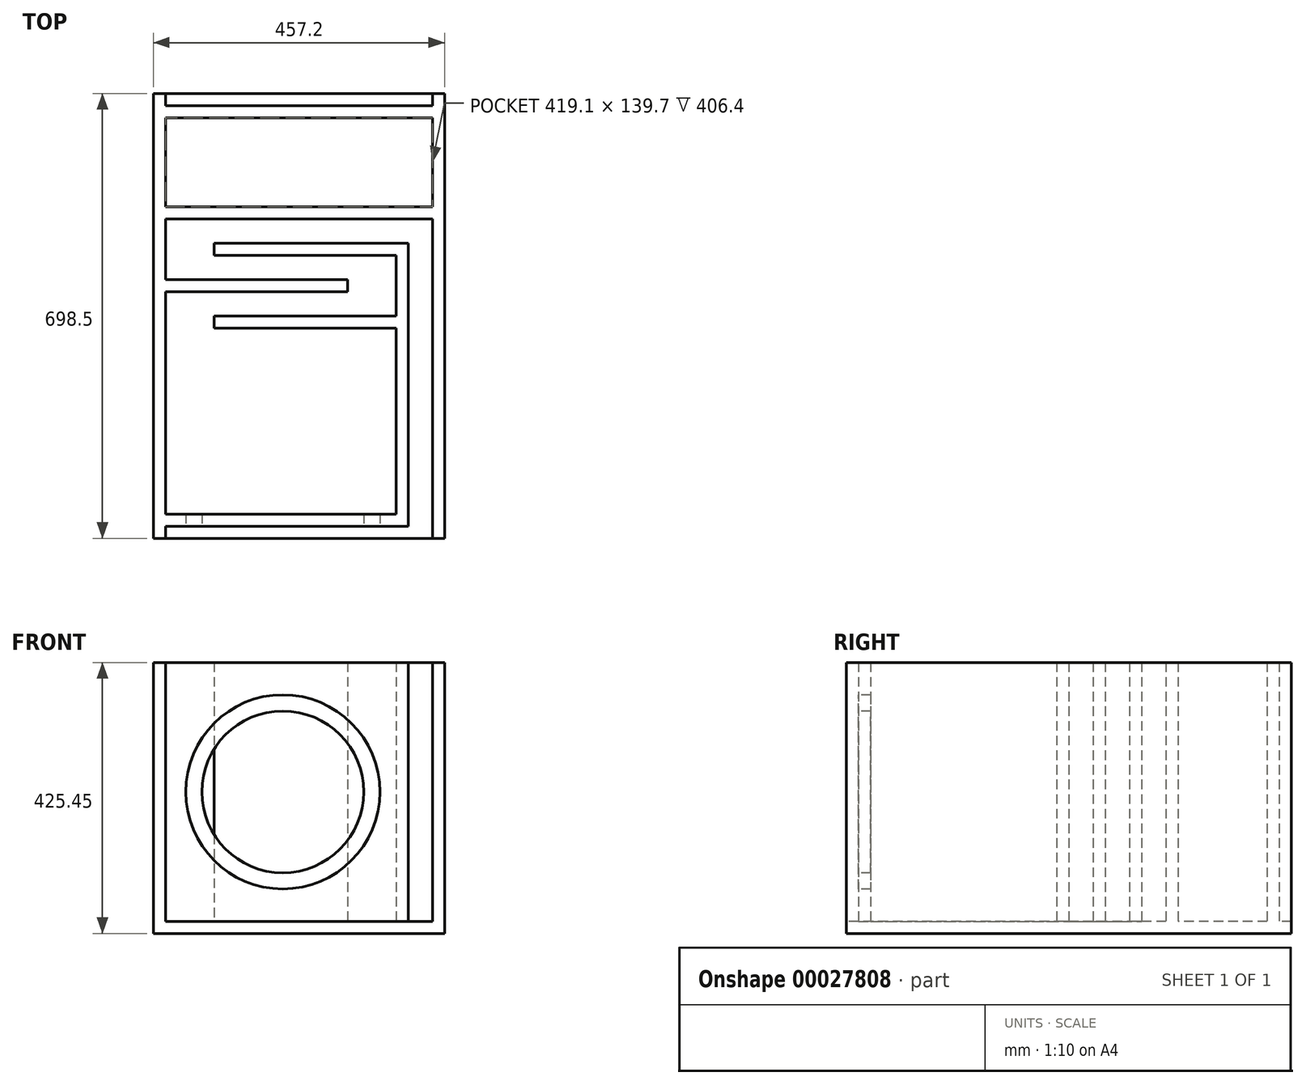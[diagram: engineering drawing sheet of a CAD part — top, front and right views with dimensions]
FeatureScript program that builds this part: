
annotation { "Feature Type Name" : "Feature", "Feature Type Description" : "" }
export const myFeature = defineFeature(function(context is Context, id is Id, definition is map)
    precondition{}
    {
        {
            var Q0;
            Q0=qCreatedBy(makeId("Top.planeOp"),FACE);
            var sketch = newSketch(context, id + "F0", { "sketchPlane" : qUnion([Q0])});
            skLineSegment(sketch, "E0.rect.bottom", {"start": v(228.6, 254) * mm, "end": v(-228.6, 254) * mm});
            skLineSegment(sketch, "E0.rect.top", {"start": v(228.6, -254) * mm, "end": v(-228.6, -254) * mm});
            skLineSegment(sketch, "E0.rect.left", {"start": v(228.6, 254) * mm, "end": v(228.6, -254) * mm});
            skLineSegment(sketch, "E0.rect.right", {"start": v(-228.6, 254) * mm, "end": v(-228.6, -254) * mm});
            skPoint(sketch, "E0.rect.middle", {"position": v(0, 0) * mm});
            skSolve(sketch);
        }
        {
            var Q0;
            Q0=makeQuery(id+"F0.imprint","IMPRINT",FACE,{"disambiguationData":[TD([[makeQuery(id+"F0.imprint","IMPRINT",EDGE,{"derivedFrom":sQuery(id+"F0.wireOp",EDGE,"E0.rect.bottom")}),1.0]])]});
            extrude(context, id + "F1", {"entities" : qUnion([Q0]), "depth" : 19.05 * mm});
        }
        {
            var Q0;
            Q0=makeQuery(id+"F1.opExtrude","CAP_FACE",FACE,{"disambiguationData":[OSD([sQuery(id+"F0.wireOp",EDGE,"E0.rect.bottom"),sQuery(id+"F0.wireOp",EDGE,"E0.rect.top"),sQuery(id+"F0.wireOp",EDGE,"E0.rect.left"),sQuery(id+"F0.wireOp",EDGE,"E0.rect.right")])],"isStart":false});
            var sketch = newSketch(context, id + "F2", { "sketchPlane" : qUnion([Q0])});
            skLineSegment(sketch, "E1.bottom", {"start": v(-228.6, 254) * mm, "end": v(-209.55, 254) * mm});
            skLineSegment(sketch, "E1.top", {"start": v(-228.6, -254) * mm, "end": v(-209.55, -254) * mm});
            skLineSegment(sketch, "E1.left", {"start": v(-228.6, 254) * mm, "end": v(-228.6, -254) * mm});
            skLineSegment(sketch, "E1.right", {"start": v(-209.55, 254) * mm, "end": v(-209.55, -254) * mm});
            skLineSegment(sketch, "E2.bottom", {"start": v(228.6, 254) * mm, "end": v(209.55, 254) * mm});
            skLineSegment(sketch, "E2.top", {"start": v(228.6, -254) * mm, "end": v(209.55, -254) * mm});
            skLineSegment(sketch, "E2.left", {"start": v(228.6, 254) * mm, "end": v(228.6, -254) * mm});
            skLineSegment(sketch, "E2.right", {"start": v(209.55, 254) * mm, "end": v(209.55, -254) * mm});
            skSolve(sketch);
        }
        {
            var Q0;
            Q0=makeQuery(id+"F2.imprint","IMPRINT",FACE,{"disambiguationData":[TD([[makeQuery(id+"F2.imprint","IMPRINT",EDGE,{"derivedFrom":sQuery(id+"F2.wireOp",EDGE,"E1.bottom")}),1.0]])]});
            var Q1;
            Q1=makeQuery(id+"F2.imprint","IMPRINT",FACE,{"disambiguationData":[TD([[makeQuery(id+"F2.imprint","IMPRINT",EDGE,{"derivedFrom":sQuery(id+"F2.wireOp",EDGE,"E2.bottom")}),1.0]])]});
            extrude(context, id + "F3", {"entities" : qUnion([Q0, Q1]), "operationType" : NewBodyOperationType.ADD, "depth" : 406.4 * mm});
        }
        {
            var Q0;
            Q0=makeQuery(id+"F1.opExtrude","CAP_FACE",FACE,{"disambiguationData":[OSD([sQuery(id+"F0.wireOp",EDGE,"E0.rect.bottom"),sQuery(id+"F0.wireOp",EDGE,"E0.rect.top"),sQuery(id+"F0.wireOp",EDGE,"E0.rect.left"),sQuery(id+"F0.wireOp",EDGE,"E0.rect.right")])],"isStart":false});
            var sketch = newSketch(context, id + "F4", { "sketchPlane" : qUnion([Q0])});
            skLineSegment(sketch, "E3.bottom", {"start": v(-209.55, 234.95) * mm, "end": v(209.55, 234.95) * mm});
            skLineSegment(sketch, "E3.top", {"start": v(-209.55, 215.9) * mm, "end": v(209.55, 215.9) * mm});
            skLineSegment(sketch, "E3.left", {"start": v(-209.55, 234.95) * mm, "end": v(-209.55, 215.9) * mm});
            skLineSegment(sketch, "E3.right", {"start": v(209.55, 234.95) * mm, "end": v(209.55, 215.9) * mm});
            skSolve(sketch);
        }
        {
            var Q0;
            Q0=makeQuery(id+"F4.imprint","IMPRINT",FACE,{"disambiguationData":[TD([[makeQuery(id+"F4.imprint","IMPRINT",EDGE,{"derivedFrom":sQuery(id+"F4.wireOp",EDGE,"E3.bottom")}),-1.0]])]});
            extrude(context, id + "F5", {"entities" : qUnion([Q0]), "operationType" : NewBodyOperationType.ADD, "depth" : 406.4 * mm});
        }
        {
            var Q0;
            {var subQ0=sQuery(id+"F0.wireOp",EDGE,"E0.rect.top");Q0=makeQuery(id+"F5.boolean.opBoolean","SPLIT",FACE,{"disambiguationData":[TD([makeQuery(id+"F1.opExtrude","SWEPT_FACE",FACE,{"disambiguationData":[OSD([subQ0])]})])],"derivedFrom":makeQuery(id+"F1.opExtrude","CAP_FACE",FACE,{"disambiguationData":[OSD([sQuery(id+"F0.wireOp",EDGE,"E0.rect.bottom"),subQ0,sQuery(id+"F0.wireOp",EDGE,"E0.rect.left"),sQuery(id+"F0.wireOp",EDGE,"E0.rect.right")])],"isStart":false})});}
            var sketch = newSketch(context, id + "F6", { "sketchPlane" : qUnion([Q0])});
            skLineSegment(sketch, "E4.bottom", {"start": v(-209.55, -215.9) * mm, "end": v(209.55, -215.9) * mm});
            skLineSegment(sketch, "E4.top", {"start": v(-209.55, -234.95) * mm, "end": v(209.55, -234.95) * mm});
            skLineSegment(sketch, "E4.left", {"start": v(-209.55, -215.9) * mm, "end": v(-209.55, -234.95) * mm});
            skLineSegment(sketch, "E4.right", {"start": v(209.55, -215.9) * mm, "end": v(209.55, -234.95) * mm});
            skSolve(sketch);
        }
        {
            var Q0;
            Q0=makeQuery(id+"F6.imprint","IMPRINT",FACE,{"disambiguationData":[TD([[makeQuery(id+"F6.imprint","IMPRINT",EDGE,{"derivedFrom":sQuery(id+"F6.wireOp",EDGE,"E4.bottom")}),-1.0]])]});
            extrude(context, id + "F7", {"entities" : qUnion([Q0]), "operationType" : NewBodyOperationType.ADD, "depth" : 406.4 * mm});
        }
        {
            var Q0;
            {var subQ0=sQuery(id+"F0.wireOp",EDGE,"E0.rect.top");var subQ1=makeQuery(id+"F5.opExtrude","SWEPT_FACE",FACE,{"disambiguationData":[OSD([sQuery(id+"F4.wireOp",EDGE,"E3.top")])]});Q0=makeQuery(id+"F7.boolean.opBoolean","SPLIT",FACE,{"disambiguationData":[TD([subQ1])],"derivedFrom":makeQuery(id+"F5.boolean.opBoolean","SPLIT",FACE,{"disambiguationData":[TD([makeQuery(id+"F1.opExtrude","SWEPT_FACE",FACE,{"disambiguationData":[OSD([subQ0])]})])],"derivedFrom":makeQuery(id+"F1.opExtrude","CAP_FACE",FACE,{"disambiguationData":[OSD([sQuery(id+"F0.wireOp",EDGE,"E0.rect.bottom"),subQ0,sQuery(id+"F0.wireOp",EDGE,"E0.rect.left"),sQuery(id+"F0.wireOp",EDGE,"E0.rect.right")])],"isStart":false})})});}
            var sketch = newSketch(context, id + "F8", { "sketchPlane" : qUnion([Q0])});
            skLineSegment(sketch, "E5.bottom", {"start": v(171.45, -215.9) * mm, "end": v(152.4, -215.9) * mm});
            skLineSegment(sketch, "E5.top", {"start": v(171.45, 82.55) * mm, "end": v(152.4, 82.55) * mm});
            skLineSegment(sketch, "E5.left", {"start": v(171.45, -215.9) * mm, "end": v(171.45, 82.55) * mm});
            skLineSegment(sketch, "E5.right", {"start": v(152.4, -215.9) * mm, "end": v(152.4, 82.55) * mm});
            skLineSegment(sketch, "E6.bottom", {"start": v(152.4, 82.55) * mm, "end": v(-133.35, 82.55) * mm});
            skLineSegment(sketch, "E6.top", {"start": v(152.4, 63.5) * mm, "end": v(-133.35, 63.5) * mm});
            skLineSegment(sketch, "E6.left", {"start": v(152.4, 82.55) * mm, "end": v(152.4, 63.5) * mm});
            skLineSegment(sketch, "E6.right", {"start": v(-133.35, 82.55) * mm, "end": v(-133.35, 63.5) * mm});
            skLineSegment(sketch, "E7.bottom", {"start": v(-209.55, 25.4) * mm, "end": v(76.2, 25.4) * mm});
            skLineSegment(sketch, "E7.top", {"start": v(-209.55, 6.35) * mm, "end": v(76.2, 6.35) * mm});
            skLineSegment(sketch, "E7.left", {"start": v(-209.55, 25.4) * mm, "end": v(-209.55, 6.35) * mm});
            skLineSegment(sketch, "E7.right", {"start": v(76.2, 25.4) * mm, "end": v(76.2, 6.35) * mm});
            skLineSegment(sketch, "E8.bottom", {"start": v(152.4, -31.75) * mm, "end": v(-133.35, -31.75) * mm});
            skLineSegment(sketch, "E8.top", {"start": v(152.4, -50.8) * mm, "end": v(-133.35, -50.8) * mm});
            skLineSegment(sketch, "E8.left", {"start": v(152.4, -31.75) * mm, "end": v(152.4, -50.8) * mm});
            skLineSegment(sketch, "E8.right", {"start": v(-133.35, -31.75) * mm, "end": v(-133.35, -50.8) * mm});
            skSolve(sketch);
        }
        {
            var Q0;
            Q0=makeQuery(id+"F8.imprint","IMPRINT",FACE,{"disambiguationData":[TD([[makeQuery(id+"F8.imprint","IMPRINT",EDGE,{"derivedFrom":sQuery(id+"F8.wireOp",EDGE,"E6.bottom")}),1.0]])]});
            var Q1;
            Q1=makeQuery(id+"F8.imprint","IMPRINT",FACE,{"disambiguationData":[TD([[makeQuery(id+"F8.imprint","IMPRINT",EDGE,{"derivedFrom":sQuery(id+"F8.wireOp",EDGE,"E7.bottom")}),-1.0]])]});
            var Q2;
            Q2=makeQuery(id+"F8.imprint","IMPRINT",FACE,{"disambiguationData":[TD([[makeQuery(id+"F8.imprint","IMPRINT",EDGE,{"derivedFrom":sQuery(id+"F8.wireOp",EDGE,"E8.bottom")}),1.0]])]});
            var Q3;
            {var subQ3=sQuery(id+"F8.wireOp",EDGE,"E5.bottom");Q3=makeQuery(id+"F8.imprint","IMPRINT",FACE,{"disambiguationData":[TD([[makeQuery(id+"F8.imprint","IMPRINT",EDGE,{"derivedFrom":subQ3}),1.0]])]});}
            extrude(context, id + "F9", {"entities" : qUnion([Q0, Q1, Q2, Q3]), "operationType" : NewBodyOperationType.ADD, "depth" : 406.4 * mm});
        }
        {
            var Q0;
            Q0=makeQuery(id+"F9.boolean.opBoolean","MERGE",FACE,{"derivedFrom":[makeQuery(id+"F7.boolean.opBoolean","MERGE",FACE,{"derivedFrom":[makeQuery(id+"F5.boolean.opBoolean","MERGE",FACE,{"derivedFrom":[makeQuery(id+"F3.opExtrude","CAP_FACE",FACE,{"disambiguationData":[OSD([sQuery(id+"F2.wireOp",EDGE,"E1.bottom"),sQuery(id+"F2.wireOp",EDGE,"E1.top"),sQuery(id+"F2.wireOp",EDGE,"E1.left"),sQuery(id+"F2.wireOp",EDGE,"E1.right")])],"isStart":false}),makeQuery(id+"F3.opExtrude","CAP_FACE",FACE,{"disambiguationData":[OSD([sQuery(id+"F2.wireOp",EDGE,"E2.bottom"),sQuery(id+"F2.wireOp",EDGE,"E2.top"),sQuery(id+"F2.wireOp",EDGE,"E2.left"),sQuery(id+"F2.wireOp",EDGE,"E2.right")])],"isStart":false}),makeQuery(id+"F5.opExtrude","CAP_FACE",FACE,{"disambiguationData":[OSD([sQuery(id+"F4.wireOp",EDGE,"E3.bottom"),sQuery(id+"F4.wireOp",EDGE,"E3.top"),sQuery(id+"F4.wireOp",EDGE,"E3.left"),sQuery(id+"F4.wireOp",EDGE,"E3.right")])],"isStart":false})]}),makeQuery(id+"F7.opExtrude","CAP_FACE",FACE,{"disambiguationData":[OSD([sQuery(id+"F6.wireOp",EDGE,"E4.bottom"),sQuery(id+"F6.wireOp",EDGE,"E4.top"),sQuery(id+"F6.wireOp",EDGE,"E4.left"),sQuery(id+"F6.wireOp",EDGE,"E4.right")])],"isStart":false})]}),makeQuery(id+"F9.opExtrude","CAP_FACE",FACE,{"disambiguationData":[OSD([sQuery(id+"F8.wireOp",EDGE,"E5.bottom"),sQuery(id+"F8.wireOp",EDGE,"E5.top"),sQuery(id+"F8.wireOp",EDGE,"E5.left"),sQuery(id+"F8.wireOp",EDGE,"E5.right"),sQuery(id+"F8.wireOp",EDGE,"E6.bottom"),sQuery(id+"F8.wireOp",EDGE,"E6.top"),sQuery(id+"F8.wireOp",EDGE,"E6.right"),sQuery(id+"F8.wireOp",EDGE,"E8.bottom"),sQuery(id+"F8.wireOp",EDGE,"E8.top"),sQuery(id+"F8.wireOp",EDGE,"E8.right")])],"isStart":false}),makeQuery(id+"F9.opExtrude","CAP_FACE",FACE,{"disambiguationData":[OSD([sQuery(id+"F8.wireOp",EDGE,"E7.bottom"),sQuery(id+"F8.wireOp",EDGE,"E7.top"),sQuery(id+"F8.wireOp",EDGE,"E7.left"),sQuery(id+"F8.wireOp",EDGE,"E7.right")])],"isStart":false})]});
            var sketch = newSketch(context, id + "F10", { "sketchPlane" : qUnion([Q0])});
            skLineSegment(sketch, "E9.bottom", {"start": v(-209.55, -215.9) * mm, "end": v(209.55, -215.9) * mm});
            skLineSegment(sketch, "E9.top", {"start": v(-209.55, -234.95) * mm, "end": v(209.55, -234.95) * mm});
            skLineSegment(sketch, "E9.left", {"start": v(-209.55, -215.9) * mm, "end": v(-209.55, -234.95) * mm});
            skLineSegment(sketch, "E9.right", {"start": v(209.55, -215.9) * mm, "end": v(209.55, -234.95) * mm});
            skSolve(sketch);
        }
        {
            var Q0;
            Q0=makeQuery(id+"F10.imprint","IMPRINT",FACE,{"disambiguationData":[TD([[makeQuery(id+"F10.imprint","IMPRINT",EDGE,{"derivedFrom":sQuery(id+"F10.wireOp",EDGE,"E9.top")}),1.0]])]});
            extrude(context, id + "F11", {"entities" : qUnion([Q0]), "operationType" : NewBodyOperationType.REMOVE, "oppositeDirection" : true, "depth" : 406.4 * mm});
        }
        {
            var Q0;
            Q0=makeQuery(id+"F3.boolean.opBoolean","MERGE",FACE,{"derivedFrom":[makeQuery(id+"F1.opExtrude","SWEPT_FACE",FACE,{"disambiguationData":[OSD([sQuery(id+"F0.wireOp",EDGE,"E0.rect.top")])]}),makeQuery(id+"F3.opExtrude","SWEPT_FACE",FACE,{"disambiguationData":[OSD([sQuery(id+"F2.wireOp",EDGE,"E1.top")])]}),makeQuery(id+"F3.opExtrude","SWEPT_FACE",FACE,{"disambiguationData":[OSD([sQuery(id+"F2.wireOp",EDGE,"E2.top")])]})]});
            extrude(context, id + "F12", {"entities" : qUnion([Q0]), "operationType" : NewBodyOperationType.ADD, "depth" : 127 * mm});
        }
        {
            var Q0;
            Q0=makeQuery(id+"F11.boolean.opBoolean","COPY",FACE,{"derivedFrom":makeQuery(id+"F11.opExtrude","SWEPT_FACE",FACE,{"disambiguationData":[OSD([sQuery(id+"F10.wireOp",EDGE,"E9.bottom")])]})});
            extrude(context, id + "F13", {"entities" : qUnion([Q0]), "operationType" : NewBodyOperationType.ADD, "depth" : 127 * mm});
        }
        {
            var Q0;
            {var subQ0=sQuery(id+"F0.wireOp",EDGE,"E0.rect.top");var subQ1=makeQuery(id+"F5.opExtrude","SWEPT_FACE",FACE,{"disambiguationData":[OSD([sQuery(id+"F4.wireOp",EDGE,"E3.top")])]});var subQ6=makeQuery(id+"F1.opExtrude","SWEPT_FACE",FACE,{"disambiguationData":[OSD([subQ0])]});var subQ7=makeQuery(id+"F5.boolean.opBoolean","SPLIT",FACE,{"disambiguationData":[TD([subQ6])],"derivedFrom":makeQuery(id+"F1.opExtrude","CAP_FACE",FACE,{"disambiguationData":[OSD([sQuery(id+"F0.wireOp",EDGE,"E0.rect.bottom"),subQ0,sQuery(id+"F0.wireOp",EDGE,"E0.rect.left"),sQuery(id+"F0.wireOp",EDGE,"E0.rect.right")])],"isStart":false})});Q0=makeQuery(id+"F12.boolean.opBoolean","MERGE",FACE,{"derivedFrom":[makeQuery(id+"F11.boolean.opBoolean","MERGE",FACE,{"derivedFrom":[makeQuery(id+"F7.boolean.opBoolean","SPLIT",FACE,{"disambiguationData":[TD([subQ6])],"derivedFrom":subQ7}),makeQuery(id+"F7.boolean.opBoolean","SPLIT",FACE,{"disambiguationData":[TD([subQ1])],"derivedFrom":subQ7}),makeQuery(id+"F11.opExtrude","CAP_FACE",FACE,{"disambiguationData":[OSD([sQuery(id+"F10.wireOp",EDGE,"E9.bottom"),sQuery(id+"F10.wireOp",EDGE,"E9.top"),sQuery(id+"F10.wireOp",EDGE,"E9.left"),sQuery(id+"F10.wireOp",EDGE,"E9.right")])],"isStart":false})]}),makeQuery(id+"F12.opExtrude","SWEPT_FACE",FACE,{"disambiguationData":[OSD([subQ0]),TDD([makeQuery(id+"F1.opExtrude","CAP_EDGE",EDGE,{"disambiguationData":[OSD([subQ0])],"isStart":false})])]})]});}
            var sketch = newSketch(context, id + "F14", { "sketchPlane" : qUnion([Q0])});
            skLineSegment(sketch, "E10.bottom", {"start": v(171.45, -342.9) * mm, "end": v(-209.55, -342.9) * mm});
            skLineSegment(sketch, "E10.top", {"start": v(171.45, -361.95) * mm, "end": v(-209.55, -361.95) * mm});
            skLineSegment(sketch, "E10.left", {"start": v(171.45, -342.9) * mm, "end": v(171.45, -361.95) * mm});
            skLineSegment(sketch, "E10.right", {"start": v(-209.55, -342.9) * mm, "end": v(-209.55, -361.95) * mm});
            skSolve(sketch);
        }
        {
            var Q0;
            Q0=makeQuery(id+"F14.imprint","IMPRINT",FACE,{"disambiguationData":[TD([[makeQuery(id+"F14.imprint","IMPRINT",EDGE,{"derivedFrom":sQuery(id+"F14.wireOp",EDGE,"E10.top")}),-1.0]])]});
            extrude(context, id + "F15", {"entities" : qUnion([Q0]), "operationType" : NewBodyOperationType.ADD, "depth" : 406.4 * mm});
        }
        {
            var Q0;
            Q0=makeQuery(id+"F15.opExtrude","SWEPT_FACE",FACE,{"disambiguationData":[OSD([sQuery(id+"F14.wireOp",EDGE,"E10.top")])]});
            var sketch = newSketch(context, id + "F16", { "sketchPlane" : qUnion([Q0])});
            skCircle(sketch, "E11", {"center": v(-25.4, 222.25) * mm, "radius": 152.4 * mm});
            skSolve(sketch);
        }
        {
            var Q0;
            Q0=makeQuery(id+"F16.imprint","IMPRINT",FACE,{"disambiguationData":[TD([[makeQuery(id+"F16.imprint","IMPRINT",EDGE,{"derivedFrom":sQuery(id+"F16.wireOp",EDGE,"E11")}),1.0]])]});
            extrude(context, id + "F17", {"entities" : qUnion([Q0]), "operationType" : NewBodyOperationType.REMOVE, "oppositeDirection" : true, "depth" : 25.4 * mm});
        }
        {
            var Q0;
            Q0=makeQuery(id+"F5.opExtrude","SWEPT_FACE",FACE,{"disambiguationData":[OSD([sQuery(id+"F4.wireOp",EDGE,"E3.bottom")])]});
            var sketch = newSketch(context, id + "F18", { "sketchPlane" : qUnion([Q0])});
            skLineSegment(sketch, "E12.rect.bottom", {"start": v(-107.95, 349.25) * mm, "end": v(107.95, 349.25) * mm});
            skLineSegment(sketch, "E12.rect.top", {"start": v(-107.95, 133.35) * mm, "end": v(107.95, 133.35) * mm});
            skLineSegment(sketch, "E12.rect.left", {"start": v(-107.95, 349.25) * mm, "end": v(-107.95, 133.35) * mm});
            skLineSegment(sketch, "E12.rect.right", {"start": v(107.95, 349.25) * mm, "end": v(107.95, 133.35) * mm});
            skPoint(sketch, "E12.rect.middle", {"position": v(0, 241.3) * mm});
            skSolve(sketch);
        }
        {
            var Q0;
            Q0=makeQuery(id+"F18.imprint","IMPRINT",FACE,{"disambiguationData":[TD([[makeQuery(id+"F18.imprint","IMPRINT",EDGE,{"derivedFrom":sQuery(id+"F18.wireOp",EDGE,"E12.rect.bottom")}),-1.0]])]});
            extrude(context, id + "F19", {"entities" : qUnion([Q0]), "operationType" : NewBodyOperationType.REMOVE, "oppositeDirection" : true, "depth" : 25.4 * mm});
        }
        {
            var Q0;
            {var subQ0=sQuery(id+"F0.wireOp",EDGE,"E0.rect.top");var subQ1=makeQuery(id+"F5.opExtrude","SWEPT_FACE",FACE,{"disambiguationData":[OSD([sQuery(id+"F4.wireOp",EDGE,"E3.top")])]});var subQ6=makeQuery(id+"F1.opExtrude","SWEPT_FACE",FACE,{"disambiguationData":[OSD([subQ0])]});var subQ7=makeQuery(id+"F5.boolean.opBoolean","SPLIT",FACE,{"disambiguationData":[TD([subQ6])],"derivedFrom":makeQuery(id+"F1.opExtrude","CAP_FACE",FACE,{"disambiguationData":[OSD([sQuery(id+"F0.wireOp",EDGE,"E0.rect.bottom"),subQ0,sQuery(id+"F0.wireOp",EDGE,"E0.rect.left"),sQuery(id+"F0.wireOp",EDGE,"E0.rect.right")])],"isStart":false})});Q0=makeQuery(id+"F12.boolean.opBoolean","MERGE",FACE,{"derivedFrom":[makeQuery(id+"F11.boolean.opBoolean","MERGE",FACE,{"derivedFrom":[makeQuery(id+"F7.boolean.opBoolean","SPLIT",FACE,{"disambiguationData":[TD([subQ6])],"derivedFrom":subQ7}),makeQuery(id+"F7.boolean.opBoolean","SPLIT",FACE,{"disambiguationData":[TD([subQ1])],"derivedFrom":subQ7}),makeQuery(id+"F11.opExtrude","CAP_FACE",FACE,{"disambiguationData":[OSD([sQuery(id+"F10.wireOp",EDGE,"E9.bottom"),sQuery(id+"F10.wireOp",EDGE,"E9.top"),sQuery(id+"F10.wireOp",EDGE,"E9.left"),sQuery(id+"F10.wireOp",EDGE,"E9.right")])],"isStart":false})]}),makeQuery(id+"F12.opExtrude","SWEPT_FACE",FACE,{"disambiguationData":[OSD([subQ0]),TDD([makeQuery(id+"F1.opExtrude","CAP_EDGE",EDGE,{"disambiguationData":[OSD([subQ0])],"isStart":false})])]})]});}
            var sketch = newSketch(context, id + "F20", { "sketchPlane" : qUnion([Q0])});
            skLineSegment(sketch, "E13.bottom", {"start": v(-209.55, 120.65) * mm, "end": v(209.55, 120.65) * mm});
            skLineSegment(sketch, "E13.top", {"start": v(-209.55, 139.7) * mm, "end": v(209.55, 139.7) * mm});
            skLineSegment(sketch, "E13.left", {"start": v(-209.55, 120.65) * mm, "end": v(-209.55, 139.7) * mm});
            skLineSegment(sketch, "E13.right", {"start": v(209.55, 120.65) * mm, "end": v(209.55, 139.7) * mm});
            skSolve(sketch);
        }
        {
            var Q0;
            Q0=makeQuery(id+"F20.imprint","IMPRINT",FACE,{"disambiguationData":[TD([[makeQuery(id+"F20.imprint","IMPRINT",EDGE,{"derivedFrom":sQuery(id+"F20.wireOp",EDGE,"E13.bottom")}),1.0]])]});
            extrude(context, id + "F21", {"entities" : qUnion([Q0]), "operationType" : NewBodyOperationType.ADD, "depth" : 406.4 * mm});
        }
        {
            var Q0;
            {var subQ0=sQuery(id+"F2.wireOp",EDGE,"E1.bottom");var subQ1=sQuery(id+"F2.wireOp",EDGE,"E1.top");var subQ2=sQuery(id+"F2.wireOp",EDGE,"E1.left");var subQ3=sQuery(id+"F2.wireOp",EDGE,"E1.right");var subQ4=sQuery(id+"F2.wireOp",EDGE,"E2.bottom");var subQ5=sQuery(id+"F2.wireOp",EDGE,"E2.top");var subQ6=sQuery(id+"F2.wireOp",EDGE,"E2.left");var subQ7=sQuery(id+"F2.wireOp",EDGE,"E2.right");var subQ8=sQuery(id+"F4.wireOp",EDGE,"E3.bottom");var subQ9=sQuery(id+"F4.wireOp",EDGE,"E3.top");var subQ10=sQuery(id+"F6.wireOp",EDGE,"E4.bottom");var subQ11=sQuery(id+"F8.wireOp",EDGE,"E5.bottom");var subQ12=sQuery(id+"F8.wireOp",EDGE,"E5.top");var subQ13=sQuery(id+"F8.wireOp",EDGE,"E5.left");var subQ14=sQuery(id+"F8.wireOp",EDGE,"E5.right");var subQ15=sQuery(id+"F8.wireOp",EDGE,"E6.bottom");var subQ16=sQuery(id+"F8.wireOp",EDGE,"E6.top");var subQ17=sQuery(id+"F8.wireOp",EDGE,"E6.right");var subQ18=sQuery(id+"F8.wireOp",EDGE,"E8.bottom");var subQ19=sQuery(id+"F8.wireOp",EDGE,"E8.top");var subQ20=sQuery(id+"F8.wireOp",EDGE,"E8.right");var subQ21=sQuery(id+"F8.wireOp",EDGE,"E7.bottom");var subQ22=sQuery(id+"F8.wireOp",EDGE,"E7.top");var subQ23=sQuery(id+"F8.wireOp",EDGE,"E7.right");var subQ24=makeQuery(id+"F9.boolean.opBoolean","MERGE",FACE,{"derivedFrom":[makeQuery(id+"F7.boolean.opBoolean","MERGE",FACE,{"derivedFrom":[makeQuery(id+"F5.boolean.opBoolean","MERGE",FACE,{"derivedFrom":[makeQuery(id+"F3.opExtrude","CAP_FACE",FACE,{"disambiguationData":[OSD([subQ0,subQ1,subQ2,subQ3])],"isStart":false}),makeQuery(id+"F3.opExtrude","CAP_FACE",FACE,{"disambiguationData":[OSD([subQ4,subQ5,subQ6,subQ7])],"isStart":false}),makeQuery(id+"F5.opExtrude","CAP_FACE",FACE,{"disambiguationData":[OSD([subQ8,subQ9,sQuery(id+"F4.wireOp",EDGE,"E3.left"),sQuery(id+"F4.wireOp",EDGE,"E3.right")])],"isStart":false})]}),makeQuery(id+"F7.opExtrude","CAP_FACE",FACE,{"disambiguationData":[OSD([subQ10,sQuery(id+"F6.wireOp",EDGE,"E4.top"),sQuery(id+"F6.wireOp",EDGE,"E4.left"),sQuery(id+"F6.wireOp",EDGE,"E4.right")])],"isStart":false})]}),makeQuery(id+"F9.opExtrude","CAP_FACE",FACE,{"disambiguationData":[OSD([subQ11,subQ12,subQ13,subQ14,subQ15,subQ16,subQ17,subQ18,subQ19,subQ20])],"isStart":false}),makeQuery(id+"F9.opExtrude","CAP_FACE",FACE,{"disambiguationData":[OSD([subQ21,subQ22,sQuery(id+"F8.wireOp",EDGE,"E7.left"),subQ23])],"isStart":false})]});var subQ25=sQuery(id+"F10.wireOp",EDGE,"E9.bottom");Q0=makeQuery(id+"F21.boolean.opBoolean","MERGE",FACE,{"derivedFrom":[makeQuery(id+"F15.boolean.opBoolean","MERGE",FACE,{"derivedFrom":[makeQuery(id+"F12.boolean.opBoolean","MERGE",FACE,{"derivedFrom":[makeQuery(id+"F11.boolean.opBoolean","SPLIT",FACE,{"disambiguationData":[TD([makeQuery(id+"F1.opExtrude","SWEPT_FACE",FACE,{"disambiguationData":[OSD([sQuery(id+"F0.wireOp",EDGE,"E0.rect.bottom")])]})])],"derivedFrom":subQ24}),makeQuery(id+"F12.opExtrude","SWEPT_FACE",FACE,{"disambiguationData":[OSD([subQ1])]}),makeQuery(id+"F12.opExtrude","SWEPT_FACE",FACE,{"disambiguationData":[OSD([subQ5])]})]}),makeQuery(id+"F13.boolean.opBoolean","MERGE",FACE,{"derivedFrom":[makeQuery(id+"F11.boolean.opBoolean","SPLIT",FACE,{"disambiguationData":[TD([makeQuery(id+"F9.opExtrude","SWEPT_FACE",FACE,{"disambiguationData":[OSD([subQ13])]})])],"derivedFrom":subQ24}),makeQuery(id+"F13.opExtrude","SWEPT_FACE",FACE,{"disambiguationData":[OSD([subQ25]),TDD([makeQuery(id+"F11.boolean.opBoolean","COPY",EDGE,{"derivedFrom":makeQuery(id+"F11.opExtrude","CAP_EDGE",EDGE,{"disambiguationData":[OSD([subQ25])],"isStart":true})})])]})]}),makeQuery(id+"F15.opExtrude","CAP_FACE",FACE,{"disambiguationData":[OSD([sQuery(id+"F14.wireOp",EDGE,"E10.bottom"),sQuery(id+"F14.wireOp",EDGE,"E10.top"),sQuery(id+"F14.wireOp",EDGE,"E10.left"),sQuery(id+"F14.wireOp",EDGE,"E10.right")])],"isStart":false})]}),makeQuery(id+"F21.opExtrude","CAP_FACE",FACE,{"disambiguationData":[OSD([sQuery(id+"F20.wireOp",EDGE,"E13.bottom"),sQuery(id+"F20.wireOp",EDGE,"E13.top"),sQuery(id+"F20.wireOp",EDGE,"E13.left"),sQuery(id+"F20.wireOp",EDGE,"E13.right")])],"isStart":false})]});}
            var sketch = newSketch(context, id + "F22", { "sketchPlane" : qUnion([Q0])});
            skLineSegment(sketch, "E14.bottom", {"start": v(-209.55, 234.95) * mm, "end": v(209.55, 234.95) * mm});
            skLineSegment(sketch, "E14.top", {"start": v(-209.55, 215.9) * mm, "end": v(209.55, 215.9) * mm});
            skLineSegment(sketch, "E14.left", {"start": v(-209.55, 234.95) * mm, "end": v(-209.55, 215.9) * mm});
            skLineSegment(sketch, "E14.right", {"start": v(209.55, 234.95) * mm, "end": v(209.55, 215.9) * mm});
            skSolve(sketch);
        }
        {
            var Q0;
            Q0=makeQuery(id+"F22.imprint","IMPRINT",FACE,{"disambiguationData":[TD([[makeQuery(id+"F22.imprint","IMPRINT",EDGE,{"derivedFrom":sQuery(id+"F22.wireOp",EDGE,"E14.bottom")}),-1.0]])]});
            extrude(context, id + "F23", {"entities" : qUnion([Q0]), "operationType" : NewBodyOperationType.REMOVE, "oppositeDirection" : true, "depth" : 406.4 * mm});
        }
        {
            var Q0;
            Q0=makeQuery(id+"F3.boolean.opBoolean","MERGE",FACE,{"derivedFrom":[makeQuery(id+"F1.opExtrude","SWEPT_FACE",FACE,{"disambiguationData":[OSD([sQuery(id+"F0.wireOp",EDGE,"E0.rect.bottom")])]}),makeQuery(id+"F3.opExtrude","SWEPT_FACE",FACE,{"disambiguationData":[OSD([sQuery(id+"F2.wireOp",EDGE,"E1.bottom")])]}),makeQuery(id+"F3.opExtrude","SWEPT_FACE",FACE,{"disambiguationData":[OSD([sQuery(id+"F2.wireOp",EDGE,"E2.bottom")])]})]});
            extrude(context, id + "F24", {"entities" : qUnion([Q0]), "operationType" : NewBodyOperationType.ADD, "depth" : 63.5 * mm});
        }
        {
            var Q0;
            {var subQ0=sQuery(id+"F0.wireOp",EDGE,"E0.rect.bottom");var subQ1=sQuery(id+"F0.wireOp",EDGE,"E0.rect.top");var subQ2=makeQuery(id+"F1.opExtrude","CAP_FACE",FACE,{"disambiguationData":[OSD([subQ0,subQ1,sQuery(id+"F0.wireOp",EDGE,"E0.rect.left"),sQuery(id+"F0.wireOp",EDGE,"E0.rect.right")])],"isStart":false});var subQ6=makeQuery(id+"F5.opExtrude","SWEPT_FACE",FACE,{"disambiguationData":[OSD([sQuery(id+"F4.wireOp",EDGE,"E3.top")])]});var subQ10=makeQuery(id+"F1.opExtrude","SWEPT_FACE",FACE,{"disambiguationData":[OSD([subQ1])]});var subQ11=makeQuery(id+"F5.boolean.opBoolean","SPLIT",FACE,{"disambiguationData":[TD([subQ10])],"derivedFrom":subQ2});var subQ12=sQuery(id+"F10.wireOp",EDGE,"E9.right");Q0=makeQuery(id+"F24.boolean.opBoolean","MERGE",FACE,{"derivedFrom":[makeQuery(id+"F23.boolean.opBoolean","MERGE",FACE,{"derivedFrom":[makeQuery(id+"F5.boolean.opBoolean","SPLIT",FACE,{"disambiguationData":[TD([makeQuery(id+"F1.opExtrude","SWEPT_FACE",FACE,{"disambiguationData":[OSD([subQ0])]})])],"derivedFrom":subQ2}),makeQuery(id+"F21.boolean.opBoolean","SPLIT",FACE,{"disambiguationData":[TD([subQ6])],"derivedFrom":makeQuery(id+"F12.boolean.opBoolean","MERGE",FACE,{"derivedFrom":[makeQuery(id+"F11.boolean.opBoolean","MERGE",FACE,{"derivedFrom":[makeQuery(id+"F7.boolean.opBoolean","SPLIT",FACE,{"disambiguationData":[TD([subQ10])],"derivedFrom":subQ11}),makeQuery(id+"F7.boolean.opBoolean","SPLIT",FACE,{"disambiguationData":[TD([subQ6])],"derivedFrom":subQ11}),makeQuery(id+"F11.opExtrude","CAP_FACE",FACE,{"disambiguationData":[OSD([sQuery(id+"F10.wireOp",EDGE,"E9.bottom"),sQuery(id+"F10.wireOp",EDGE,"E9.top"),sQuery(id+"F10.wireOp",EDGE,"E9.left"),subQ12])],"isStart":false})]}),makeQuery(id+"F12.opExtrude","SWEPT_FACE",FACE,{"disambiguationData":[OSD([subQ1]),TDD([makeQuery(id+"F1.opExtrude","CAP_EDGE",EDGE,{"disambiguationData":[OSD([subQ1])],"isStart":false})])]})]})}),makeQuery(id+"F23.opExtrude","CAP_FACE",FACE,{"disambiguationData":[OSD([sQuery(id+"F22.wireOp",EDGE,"E14.bottom"),sQuery(id+"F22.wireOp",EDGE,"E14.top"),sQuery(id+"F22.wireOp",EDGE,"E14.left"),sQuery(id+"F22.wireOp",EDGE,"E14.right")])],"isStart":false})]}),makeQuery(id+"F24.opExtrude","SWEPT_FACE",FACE,{"disambiguationData":[OSD([subQ0]),TDD([makeQuery(id+"F1.opExtrude","CAP_EDGE",EDGE,{"disambiguationData":[OSD([subQ0])],"isStart":false})])]})]});}
            var sketch = newSketch(context, id + "F25", { "sketchPlane" : qUnion([Q0])});
            skLineSegment(sketch, "E15.bottom", {"start": v(-209.55, 298.45) * mm, "end": v(209.55, 298.45) * mm});
            skLineSegment(sketch, "E15.top", {"start": v(-209.55, 279.4) * mm, "end": v(209.55, 279.4) * mm});
            skLineSegment(sketch, "E15.left", {"start": v(-209.55, 298.45) * mm, "end": v(-209.55, 279.4) * mm});
            skLineSegment(sketch, "E15.right", {"start": v(209.55, 298.45) * mm, "end": v(209.55, 279.4) * mm});
            skSolve(sketch);
        }
        {
            var Q0;
            Q0=makeQuery(id+"F25.imprint","IMPRINT",FACE,{"disambiguationData":[TD([[makeQuery(id+"F25.imprint","IMPRINT",EDGE,{"derivedFrom":sQuery(id+"F25.wireOp",EDGE,"E15.bottom")}),-1.0]])]});
            extrude(context, id + "F26", {"entities" : qUnion([Q0]), "operationType" : NewBodyOperationType.ADD, "depth" : 406.4 * mm});
        }
        {
            var Q0;
            Q0=makeQuery(id+"F15.opExtrude","SWEPT_FACE",FACE,{"disambiguationData":[OSD([sQuery(id+"F14.wireOp",EDGE,"E10.top")])]});
            var sketch = newSketch(context, id + "F27", { "sketchPlane" : qUnion([Q0])});
            skCircle(sketch, "E16", {"center": v(-25.4, 222.25) * mm, "radius": 127 * mm});
            skSolve(sketch);
        }
        {
            var Q0;
            Q0=makeQuery(id+"F27.imprint","IMPRINT",FACE,{"disambiguationData":[TD([[makeQuery(id+"F27.imprint","IMPRINT",EDGE,{"derivedFrom":sQuery(id+"F27.wireOp",EDGE,"E16")}),-1.0]])]});
            extrude(context, id + "F28", {"entities" : qUnion([Q0]), "oppositeDirection" : true, "depth" : 19.05 * mm});
        }
    });
